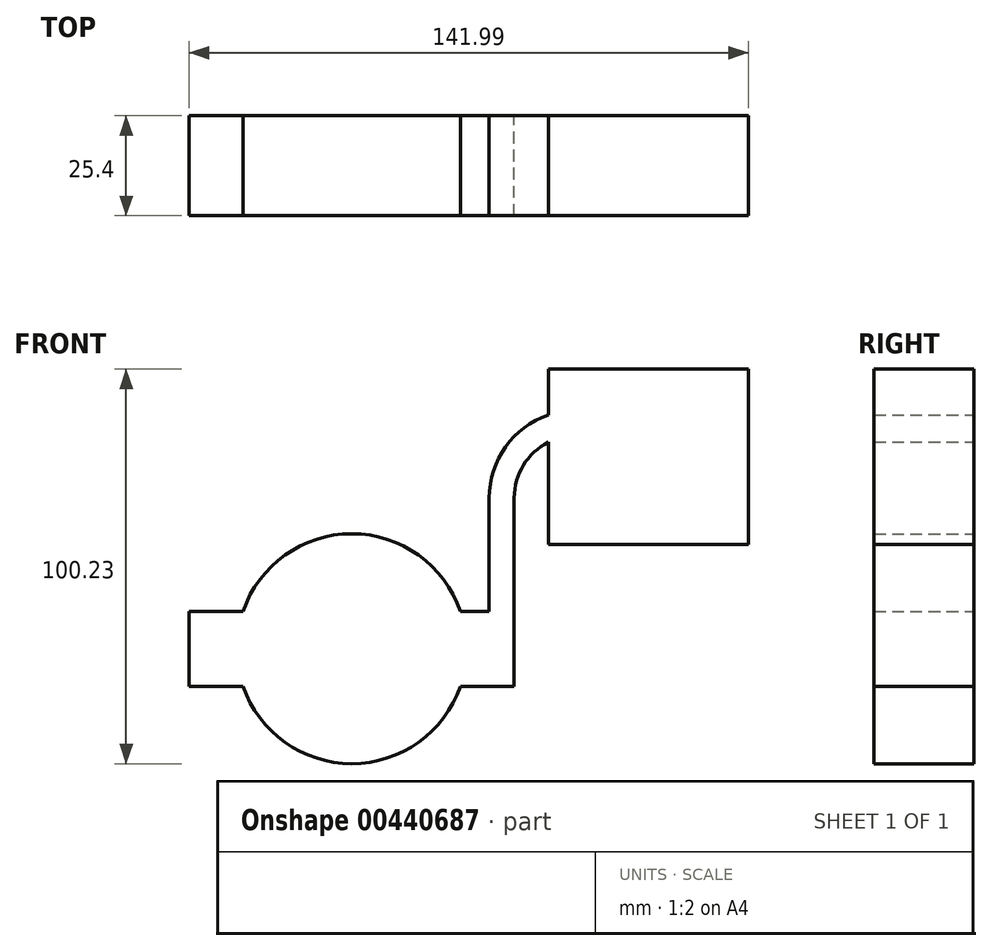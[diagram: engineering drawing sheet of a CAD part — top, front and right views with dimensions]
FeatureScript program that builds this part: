
annotation { "Feature Type Name" : "Feature", "Feature Type Description" : "" }
export const myFeature = defineFeature(function(context is Context, id is Id, definition is map)
    precondition{}
    {
        {
            var Q0;
            Q0=qCreatedBy(makeId("Front.planeOp"),FACE);
            var sketch = newSketch(context, id + "F0", { "sketchPlane" : qUnion([Q0])});
            skLineSegment(sketch, "E0.bottom", {"start": v(-41.28, 9.52) * mm, "end": v(41.27, 9.53) * mm});
            skLineSegment(sketch, "E0.top", {"start": v(-41.28, -9.53) * mm, "end": v(41.28, -9.53) * mm});
            skLineSegment(sketch, "E0.left", {"start": v(-41.28, 9.52) * mm, "end": v(-41.27, -9.53) * mm});
            skLineSegment(sketch, "E0.right", {"start": v(41.28, 9.53) * mm, "end": v(41.28, -9.52) * mm});
            skPoint(sketch, "E0.middle", {"position": v(0, 0) * mm});
            skLineSegment(sketch, "E1.bottom", {"start": v(49.92, 26.47) * mm, "end": v(100.72, 26.47) * mm});
            skLineSegment(sketch, "E1.top", {"start": v(49.92, 71.02) * mm, "end": v(100.72, 71.02) * mm});
            skLineSegment(sketch, "E1.left", {"start": v(49.92, 26.47) * mm, "end": v(49.92, 71.02) * mm});
            skLineSegment(sketch, "E1.right", {"start": v(100.72, 26.47) * mm, "end": v(100.72, 71.02) * mm});
            skPoint(sketch, "E1.middle", {"position": v(75.32, 48.74) * mm});
            skLineSegment(sketch, "E2", {"start": v(41.27, 9.53) * mm, "end": v(41.27, 38.35) * mm});
            skArc(sketch, "E3", {"start": v(41.27, 38.35) * mm, "mid": v(44.34, 47.73) * mm, "end": v(52.36, 53.49) * mm});
            skLineSegment(sketch, "E4", {"start": v(52.36, 53.49) * mm, "end": v(90.7, 53.49) * mm});
            skArc(sketch, "E5.0", {"start": v(34.92, 38.35) * mm, "mid": v(39.58, 51.96) * mm, "end": v(51.6, 59.87) * mm});
            skLineSegment(sketch, "E5.1", {"start": v(34.92, 9.53) * mm, "end": v(34.92, 38.35) * mm});
            skArc(sketch, "E6.0", {"start": v(54.09, 39.19) * mm, "mid": v(54.8, 40.5) * mm, "end": v(56.04, 41.33) * mm});
            skFitSpline(sketch, "E7", {"points": [v(8.77, 37.56) * mm, v(17.85, 42.64) * mm], "startDerivative": vector(9.08, 5.08) * mm, "endDerivative": vector(9.08, 5.08) * mm});
            skCircle(sketch, "E8", {"center": v(0, 0) * mm, "radius": 29.21 * mm});
            skSolve(sketch);
        }
        {
            var Q0;
            Q0 = qSketchRegion(id + "F0", true);
            extrude(context, id + "F1", {"entities" : qUnion([Q0]), "depth" : 25.4 * mm});
        }
        {
            var Q0;
            Q0 = qSketchRegion(id + "F0", true);
            extrude(context, id + "F2", {"entities" : qUnion([Q0]), "operationType" : NewBodyOperationType.ADD, "depth" : 25.4 * mm});
        }
        {
            var Q0;
            Q0 = qSketchRegion(id + "F0", true);
            extrude(context, id + "F3", {"entities" : qUnion([Q0]), "operationType" : NewBodyOperationType.ADD, "depth" : 25.4 * mm});
        }
        {
            var Q0;
            Q0 = qSketchRegion(id + "F0", true);
            extrude(context, id + "F4", {"entities" : qUnion([Q0]), "operationType" : NewBodyOperationType.ADD, "depth" : 25.4 * mm});
        }
    });
